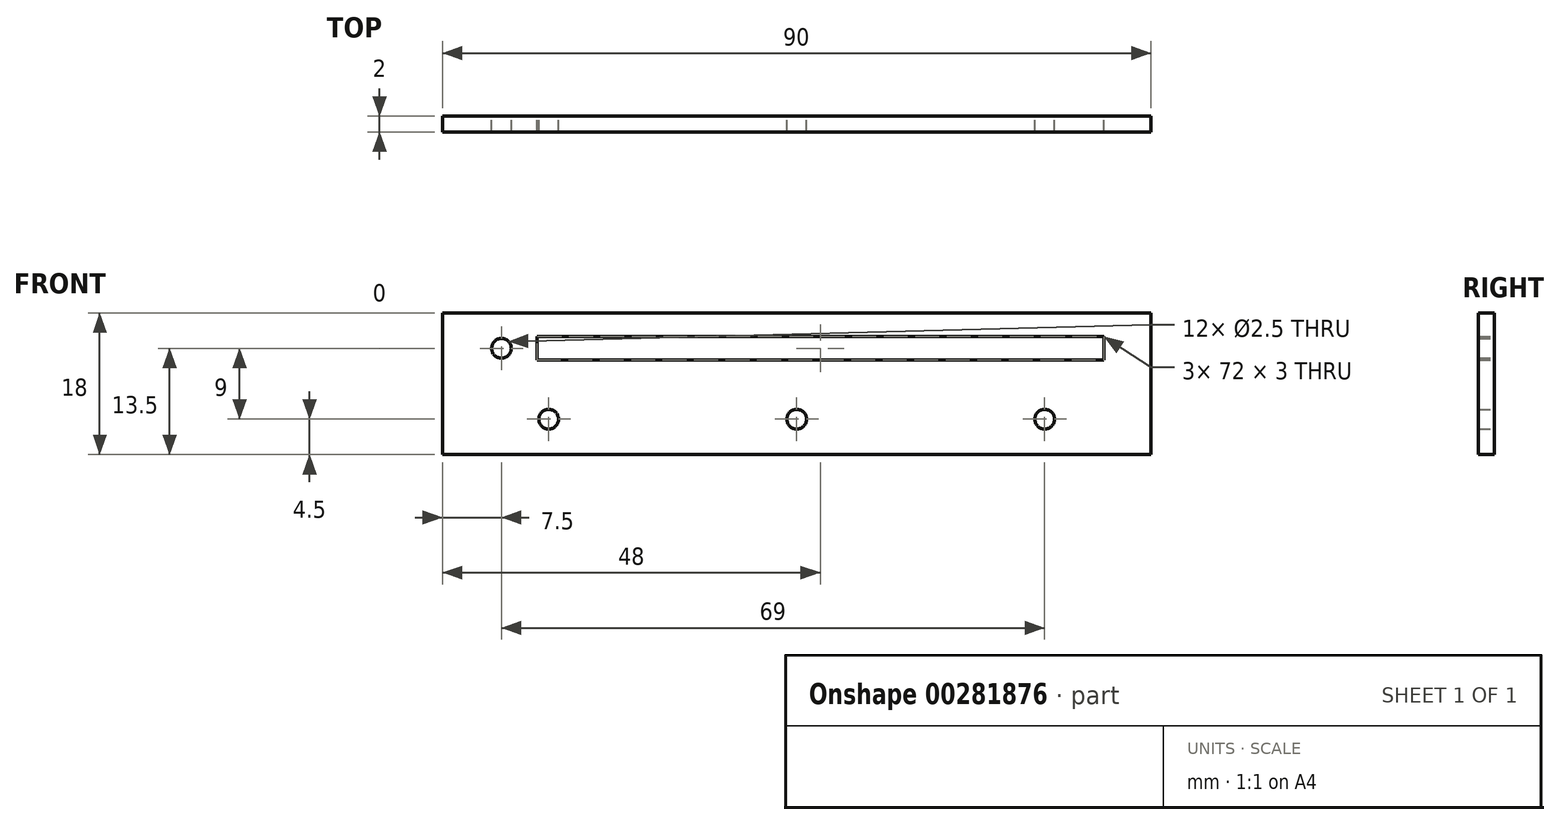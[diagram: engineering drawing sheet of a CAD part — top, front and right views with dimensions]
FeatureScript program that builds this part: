
annotation { "Feature Type Name" : "Feature", "Feature Type Description" : "" }
export const myFeature = defineFeature(function(context is Context, id is Id, definition is map)
    precondition{}
    {
        {
            var Q0;
            Q0=qCreatedBy(makeId("Front.planeOp"),FACE);
            var sketch = newSketch(context, id + "F0", { "sketchPlane" : qUnion([Q0])});
            skLineSegment(sketch, "E0.bottom", {"start": v(42, 4.5) * mm, "end": v(-42, 4.5) * mm});
            skLineSegment(sketch, "E0.top", {"start": v(42, -4.5) * mm, "end": v(-42, -4.5) * mm});
            skLineSegment(sketch, "E0.left", {"start": v(42, 4.5) * mm, "end": v(42, -4.5) * mm});
            skLineSegment(sketch, "E0.right", {"start": v(-42, 4.5) * mm, "end": v(-42, -4.5) * mm});
            skPoint(sketch, "E0.middle", {"position": v(0, 0) * mm});
            skLineSegment(sketch, "E1.bottom", {"start": v(39, 1.5) * mm, "end": v(-33, 1.5) * mm});
            skLineSegment(sketch, "E1.top", {"start": v(39, -1.5) * mm, "end": v(-33, -1.5) * mm});
            skLineSegment(sketch, "E1.left", {"start": v(39, 1.5) * mm, "end": v(39, -1.5) * mm});
            skLineSegment(sketch, "E1.right", {"start": v(-33, 1.5) * mm, "end": v(-33, -1.5) * mm});
            skCircle(sketch, "E2", {"center": v(-37.5, 0) * mm, "radius": 1.25 * mm});
            skLineSegment(sketch, "E3.bottom", {"start": v(-42, -4.5) * mm, "end": v(42, -4.5) * mm});
            skLineSegment(sketch, "E3.top", {"start": v(-42, -13.5) * mm, "end": v(42, -13.5) * mm});
            skLineSegment(sketch, "E3.left", {"start": v(-42, -4.5) * mm, "end": v(-42, -13.5) * mm});
            skLineSegment(sketch, "E3.right", {"start": v(42, -4.5) * mm, "end": v(42, -13.5) * mm});
            skCircle(sketch, "E4", {"center": v(-31.5, -9) * mm, "radius": 1.25 * mm});
            skCircle(sketch, "E5", {"center": v(0, -9) * mm, "radius": 1.25 * mm});
            skCircle(sketch, "E6", {"center": v(31.5, -9) * mm, "radius": 1.25 * mm});
            skLineSegment(sketch, "E7.bottom", {"start": v(-42, 4.5) * mm, "end": v(-45, 4.5) * mm});
            skLineSegment(sketch, "E7.top", {"start": v(-42, -13.5) * mm, "end": v(-45, -13.5) * mm});
            skLineSegment(sketch, "E7.left", {"start": v(-42, 4.5) * mm, "end": v(-42, -13.5) * mm});
            skLineSegment(sketch, "E7.right", {"start": v(-45, 4.5) * mm, "end": v(-45, -13.5) * mm});
            skLineSegment(sketch, "E8.bottom", {"start": v(42, 4.5) * mm, "end": v(45, 4.5) * mm});
            skLineSegment(sketch, "E8.top", {"start": v(42, -13.5) * mm, "end": v(45, -13.5) * mm});
            skLineSegment(sketch, "E8.left", {"start": v(42, 4.5) * mm, "end": v(42, -13.5) * mm});
            skLineSegment(sketch, "E8.right", {"start": v(45, 4.5) * mm, "end": v(45, -13.5) * mm});
            skLineSegment(sketch, "E9", {"start": v(-37.5, 0) * mm, "end": v(-37.5, -13.5) * mm, "construction": true});
            skLineSegment(sketch, "E10", {"start": v(-37.5, -13.5) * mm, "end": v(-37.5, -9) * mm, "construction": true});
            skLineSegment(sketch, "E11", {"start": v(-37.5, -9) * mm, "end": v(-31.5, -9) * mm, "construction": true});
            skSolve(sketch);
        }
        {
            var Q0;
            {var subQ2=makeQuery(id+"F0.imprint","IMPRINT",EDGE,{"derivedFrom":sQuery(id+"F0.wireOp",EDGE,"E0.top")});var subQ3=makeQuery(id+"F0.imprint","IMPRINT",EDGE,{"derivedFrom":sQuery(id+"F0.wireOp",EDGE,"E0.left")});var subQ4=makeQuery(id+"F0.imprint","IMPRINT",EDGE,{"derivedFrom":sQuery(id+"F0.wireOp",EDGE,"E0.right")});Q0=qUnion([makeQuery(id+"F0.imprint","IMPRINT",FACE,{"disambiguationData":[TD([[subQ4,-1.0]])]}),makeQuery(id+"F0.imprint","IMPRINT",FACE,{"disambiguationData":[TD([[makeQuery(id+"F0.imprint","IMPRINT",EDGE,{"derivedFrom":sQuery(id+"F0.wireOp",EDGE,"E0.bottom")}),1.0]])]}),makeQuery(id+"F0.imprint","IMPRINT",FACE,{"disambiguationData":[TD([[subQ3,1.0]])]}),makeQuery(id+"F0.imprint","IMPRINT",FACE,{"disambiguationData":[TD([[subQ2,1.0]])]})]);}
            extrude(context, id + "F1", {"entities" : qUnion([Q0]), "depth" : 2 * mm});
        }
    });
